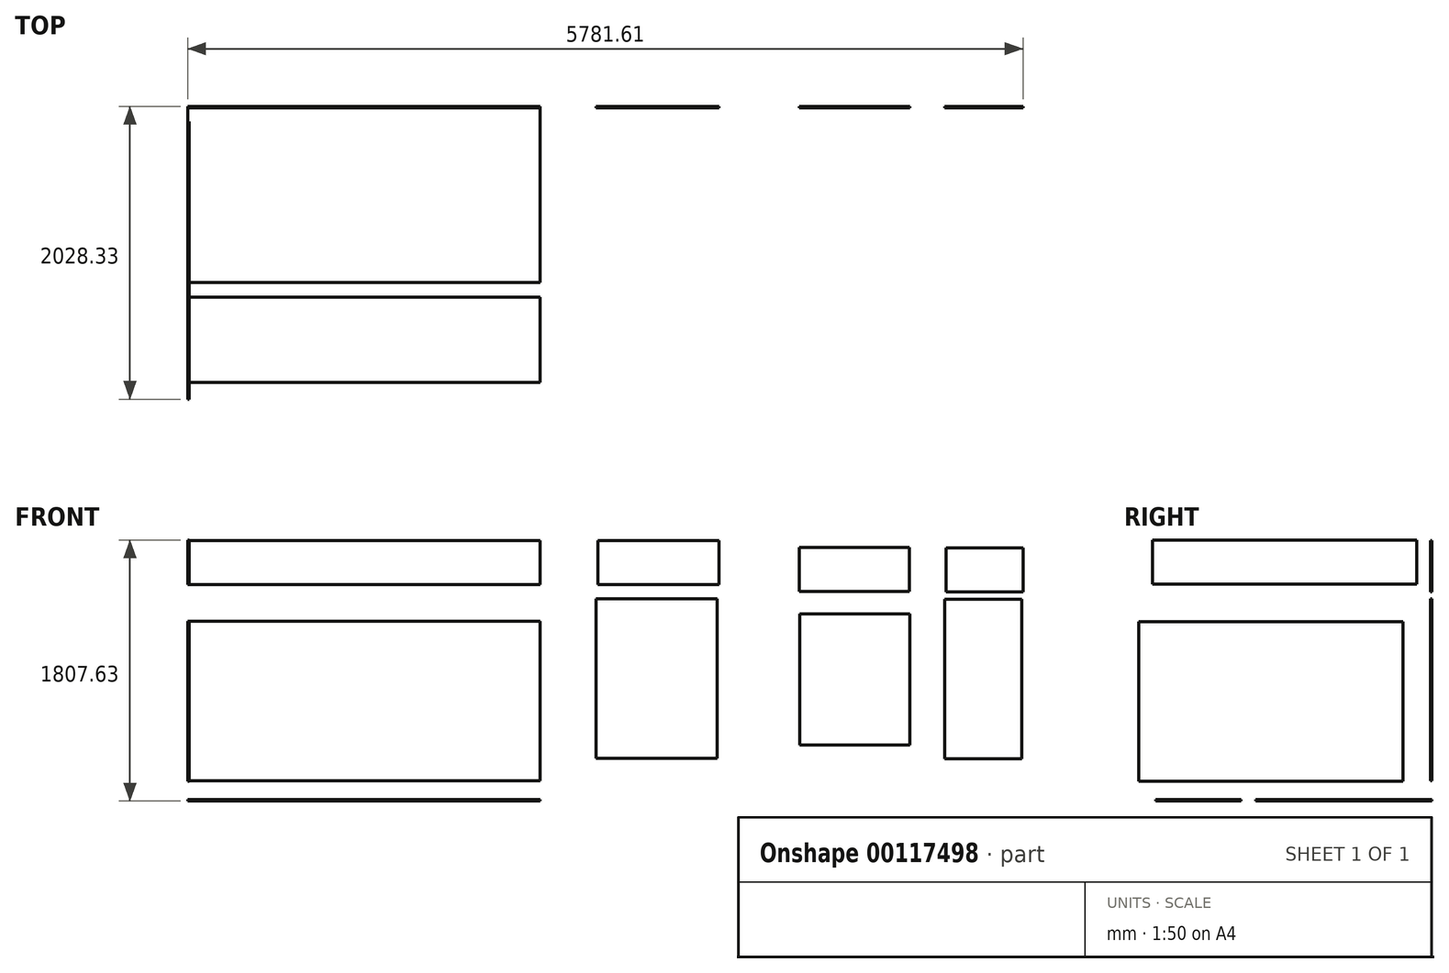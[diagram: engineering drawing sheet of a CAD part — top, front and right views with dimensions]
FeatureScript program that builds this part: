
annotation { "Feature Type Name" : "Feature", "Feature Type Description" : "" }
export const myFeature = defineFeature(function(context is Context, id is Id, definition is map)
    precondition{}
    {
        {
            var Q0;
            Q0=qCreatedBy(makeId("Top.planeOp"),FACE);
            var sketch = newSketch(context, id + "F0", { "sketchPlane" : qUnion([Q0])});
            skLineSegment(sketch, "E0.bottom", {"start": v(0, 0) * mm, "end": v(2438.4, 0) * mm});
            skLineSegment(sketch, "E0.top", {"start": v(0, -1219.2) * mm, "end": v(2438.4, -1219.2) * mm});
            skLineSegment(sketch, "E0.left", {"start": v(0, 0) * mm, "end": v(0, -1219.2) * mm});
            skLineSegment(sketch, "E0.right", {"start": v(2438.4, 0) * mm, "end": v(2438.4, -1219.2) * mm});
            skSolve(sketch);
        }
        {
            var Q0;
            Q0=makeQuery(id+"F0.imprint","IMPRINT",FACE,{"disambiguationData":[TD([[makeQuery(id+"F0.imprint","IMPRINT",EDGE,{"derivedFrom":sQuery(id+"F0.wireOp",EDGE,"E0.bottom")}),-1.0]])]});
            extrude(context, id + "F1", {"entities" : qUnion([Q0]), "depth" : 9.52 * mm});
        }
        {
            var Q0;
            Q0=qCreatedBy(makeId("Top.planeOp"),FACE);
            var sketch = newSketch(context, id + "F2", { "sketchPlane" : qUnion([Q0])});
            skLineSegment(sketch, "E1.bottom", {"start": v(0, -1320.2) * mm, "end": v(2438.4, -1320.2) * mm});
            skLineSegment(sketch, "E1.top", {"start": v(0, -1910.75) * mm, "end": v(2438.4, -1910.75) * mm});
            skLineSegment(sketch, "E1.left", {"start": v(0, -1320.2) * mm, "end": v(0, -1910.75) * mm});
            skLineSegment(sketch, "E1.right", {"start": v(2438.4, -1320.2) * mm, "end": v(2438.4, -1910.75) * mm});
            skSolve(sketch);
        }
        {
            var Q0;
            Q0=makeQuery(id+"F2.imprint","IMPRINT",FACE,{"disambiguationData":[TD([[makeQuery(id+"F2.imprint","IMPRINT",EDGE,{"derivedFrom":sQuery(id+"F2.wireOp",EDGE,"E1.bottom")}),-1.0]])]});
            extrude(context, id + "F3", {"entities" : qUnion([Q0]), "depth" : 9.52 * mm});
        }
        {
            var Q0;
            Q0=qCreatedBy(makeId("Front.planeOp"),FACE);
            var sketch = newSketch(context, id + "F4", { "sketchPlane" : qUnion([Q0])});
            skLineSegment(sketch, "E2.bottom", {"start": v(0, 139.39) * mm, "end": v(2438.4, 139.39) * mm});
            skLineSegment(sketch, "E2.top", {"start": v(0, 1244.29) * mm, "end": v(2438.4, 1244.29) * mm});
            skLineSegment(sketch, "E2.left", {"start": v(0, 139.39) * mm, "end": v(0, 1244.29) * mm});
            skLineSegment(sketch, "E2.right", {"start": v(2438.4, 139.39) * mm, "end": v(2438.4, 1244.29) * mm});
            skSolve(sketch);
        }
        {
            var Q0;
            Q0=makeQuery(id+"F4.imprint","IMPRINT",FACE,{"disambiguationData":[TD([[makeQuery(id+"F4.imprint","IMPRINT",EDGE,{"derivedFrom":sQuery(id+"F4.wireOp",EDGE,"E2.bottom")}),1.0]])]});
            extrude(context, id + "F5", {"entities" : qUnion([Q0]), "depth" : 9.52 * mm});
        }
        {
            var Q0;
            Q0=qCreatedBy(makeId("Right.planeOp"),FACE);
            var sketch = newSketch(context, id + "F6", { "sketchPlane" : qUnion([Q0])});
            skLineSegment(sketch, "E3.bottom", {"start": v(-199.53, 136.34) * mm, "end": v(-2028.33, 136.34) * mm});
            skLineSegment(sketch, "E3.top", {"start": v(-199.53, 1241.24) * mm, "end": v(-2028.33, 1241.24) * mm});
            skLineSegment(sketch, "E3.left", {"start": v(-199.53, 136.34) * mm, "end": v(-199.53, 1241.24) * mm});
            skLineSegment(sketch, "E3.right", {"start": v(-2028.33, 136.34) * mm, "end": v(-2028.33, 1241.24) * mm});
            skSolve(sketch);
        }
        {
            var Q0;
            Q0=makeQuery(id+"F6.imprint","IMPRINT",FACE,{"disambiguationData":[TD([[makeQuery(id+"F6.imprint","IMPRINT",EDGE,{"derivedFrom":sQuery(id+"F6.wireOp",EDGE,"E3.bottom")}),-1.0]])]});
            extrude(context, id + "F7", {"entities" : qUnion([Q0]), "depth" : 9.52 * mm});
        }
        {
            var Q0;
            Q0=qCreatedBy(makeId("Front.planeOp"),FACE);
            var sketch = newSketch(context, id + "F8", { "sketchPlane" : qUnion([Q0])});
            skLineSegment(sketch, "E4.bottom", {"start": v(0, 1500.5) * mm, "end": v(2438.4, 1500.5) * mm});
            skLineSegment(sketch, "E4.top", {"start": v(0, 1805.3) * mm, "end": v(2438.4, 1805.3) * mm});
            skLineSegment(sketch, "E4.left", {"start": v(0, 1500.5) * mm, "end": v(0, 1805.3) * mm});
            skLineSegment(sketch, "E4.right", {"start": v(2438.4, 1500.5) * mm, "end": v(2438.4, 1805.3) * mm});
            skSolve(sketch);
        }
        {
            var Q0;
            Q0=makeQuery(id+"F8.imprint","IMPRINT",FACE,{"disambiguationData":[TD([[makeQuery(id+"F8.imprint","IMPRINT",EDGE,{"derivedFrom":sQuery(id+"F8.wireOp",EDGE,"E4.bottom")}),1.0]])]});
            extrude(context, id + "F9", {"entities" : qUnion([Q0]), "depth" : 9.52 * mm});
        }
        {
            var Q0;
            Q0=qCreatedBy(makeId("Right.planeOp"),FACE);
            var sketch = newSketch(context, id + "F10", { "sketchPlane" : qUnion([Q0])});
            skLineSegment(sketch, "E5.bottom", {"start": v(-104.16, 1502.83) * mm, "end": v(-1932.96, 1502.83) * mm});
            skLineSegment(sketch, "E5.top", {"start": v(-104.16, 1807.63) * mm, "end": v(-1932.96, 1807.63) * mm});
            skLineSegment(sketch, "E5.left", {"start": v(-104.16, 1502.83) * mm, "end": v(-104.16, 1807.63) * mm});
            skLineSegment(sketch, "E5.right", {"start": v(-1932.96, 1502.83) * mm, "end": v(-1932.96, 1807.63) * mm});
            skSolve(sketch);
        }
        {
            var Q0;
            Q0=makeQuery(id+"F10.imprint","IMPRINT",FACE,{"disambiguationData":[TD([[makeQuery(id+"F10.imprint","IMPRINT",EDGE,{"derivedFrom":sQuery(id+"F10.wireOp",EDGE,"E5.bottom")}),-1.0]])]});
            extrude(context, id + "F11", {"entities" : qUnion([Q0]), "depth" : 9.52 * mm});
        }
        {
            var Q0;
            Q0=qCreatedBy(makeId("Front.planeOp"),FACE);
            var sketch = newSketch(context, id + "F12", { "sketchPlane" : qUnion([Q0])});
            skLineSegment(sketch, "E6.bottom", {"start": v(2827.65, 295.84) * mm, "end": v(3665.85, 295.84) * mm});
            skLineSegment(sketch, "E6.top", {"start": v(2827.65, 1400.74) * mm, "end": v(3665.85, 1400.74) * mm});
            skLineSegment(sketch, "E6.left", {"start": v(2827.65, 295.84) * mm, "end": v(2827.65, 1400.74) * mm});
            skLineSegment(sketch, "E6.right", {"start": v(3665.85, 295.84) * mm, "end": v(3665.85, 1400.74) * mm});
            skSolve(sketch);
        }
        {
            var Q0;
            Q0=makeQuery(id+"F12.imprint","IMPRINT",FACE,{"disambiguationData":[TD([[makeQuery(id+"F12.imprint","IMPRINT",EDGE,{"derivedFrom":sQuery(id+"F12.wireOp",EDGE,"E6.bottom")}),1.0]])]});
            extrude(context, id + "F13", {"entities" : qUnion([Q0]), "depth" : 9.52 * mm});
        }
        {
            var Q0;
            Q0=qCreatedBy(makeId("Front.planeOp"),FACE);
            var sketch = newSketch(context, id + "F14", { "sketchPlane" : qUnion([Q0])});
            skLineSegment(sketch, "E7.bottom", {"start": v(4236.92, 388.8) * mm, "end": v(4998.92, 388.8) * mm});
            skLineSegment(sketch, "E7.top", {"start": v(4236.92, 1296.85) * mm, "end": v(4998.92, 1296.85) * mm});
            skLineSegment(sketch, "E7.left", {"start": v(4236.92, 388.8) * mm, "end": v(4236.92, 1296.85) * mm});
            skLineSegment(sketch, "E7.right", {"start": v(4998.92, 388.8) * mm, "end": v(4998.92, 1296.85) * mm});
            skSolve(sketch);
        }
        {
            var Q0;
            Q0=makeQuery(id+"F14.imprint","IMPRINT",FACE,{"disambiguationData":[TD([[makeQuery(id+"F14.imprint","IMPRINT",EDGE,{"derivedFrom":sQuery(id+"F14.wireOp",EDGE,"E7.bottom")}),1.0]])]});
            extrude(context, id + "F15", {"entities" : qUnion([Q0]), "depth" : 9.52 * mm});
        }
        {
            var Q0;
            Q0=qCreatedBy(makeId("Front.planeOp"),FACE);
            var sketch = newSketch(context, id + "F16", { "sketchPlane" : qUnion([Q0])});
            skLineSegment(sketch, "E8.bottom", {"start": v(4233.33, 1450.39) * mm, "end": v(4995.33, 1450.39) * mm});
            skLineSegment(sketch, "E8.top", {"start": v(4233.33, 1755.19) * mm, "end": v(4995.33, 1755.19) * mm});
            skLineSegment(sketch, "E8.left", {"start": v(4233.33, 1450.39) * mm, "end": v(4233.33, 1755.19) * mm});
            skLineSegment(sketch, "E8.right", {"start": v(4995.33, 1450.39) * mm, "end": v(4995.33, 1755.19) * mm});
            skSolve(sketch);
        }
        {
            var Q0;
            Q0=makeQuery(id+"F16.imprint","IMPRINT",FACE,{"disambiguationData":[TD([[makeQuery(id+"F16.imprint","IMPRINT",EDGE,{"derivedFrom":sQuery(id+"F16.wireOp",EDGE,"E8.bottom")}),1.0]])]});
            extrude(context, id + "F17", {"entities" : qUnion([Q0]), "depth" : 9.52 * mm});
        }
        {
            var Q0;
            Q0=qCreatedBy(makeId("Front.planeOp"),FACE);
            var sketch = newSketch(context, id + "F18", { "sketchPlane" : qUnion([Q0])});
            skLineSegment(sketch, "E9.bottom", {"start": v(2839.93, 1500.6) * mm, "end": v(3678.13, 1500.6) * mm});
            skLineSegment(sketch, "E9.top", {"start": v(2839.93, 1805.4) * mm, "end": v(3678.13, 1805.4) * mm});
            skLineSegment(sketch, "E9.left", {"start": v(2839.93, 1500.6) * mm, "end": v(2839.93, 1805.4) * mm});
            skLineSegment(sketch, "E9.right", {"start": v(3678.13, 1500.6) * mm, "end": v(3678.13, 1805.4) * mm});
            skSolve(sketch);
        }
        {
            var Q0;
            Q0=makeQuery(id+"F18.imprint","IMPRINT",FACE,{"disambiguationData":[TD([[makeQuery(id+"F18.imprint","IMPRINT",EDGE,{"derivedFrom":sQuery(id+"F18.wireOp",EDGE,"E9.bottom")}),1.0]])]});
            extrude(context, id + "F19", {"entities" : qUnion([Q0]), "depth" : 9.52 * mm});
        }
        {
            var Q0;
            Q0=qCreatedBy(makeId("Front.planeOp"),FACE);
            var sketch = newSketch(context, id + "F20", { "sketchPlane" : qUnion([Q0])});
            skLineSegment(sketch, "E10.bottom", {"start": v(5248.2, 1449.3) * mm, "end": v(5781.6, 1449.3) * mm});
            skLineSegment(sketch, "E10.top", {"start": v(5248.2, 1754.1) * mm, "end": v(5781.6, 1754.1) * mm});
            skLineSegment(sketch, "E10.left", {"start": v(5248.2, 1449.3) * mm, "end": v(5248.2, 1754.1) * mm});
            skLineSegment(sketch, "E10.right", {"start": v(5781.6, 1449.3) * mm, "end": v(5781.6, 1754.1) * mm});
            skSolve(sketch);
        }
        {
            var Q0;
            Q0=makeQuery(id+"F20.imprint","IMPRINT",FACE,{"disambiguationData":[TD([[makeQuery(id+"F20.imprint","IMPRINT",EDGE,{"derivedFrom":sQuery(id+"F20.wireOp",EDGE,"E10.bottom")}),1.0]])]});
            extrude(context, id + "F21", {"entities" : qUnion([Q0]), "depth" : 9.52 * mm});
        }
        {
            var Q0;
            Q0=qCreatedBy(makeId("Front.planeOp"),FACE);
            var sketch = newSketch(context, id + "F22", { "sketchPlane" : qUnion([Q0])});
            skLineSegment(sketch, "E11.bottom", {"start": v(5238.08, 1396.07) * mm, "end": v(5771.48, 1396.07) * mm});
            skLineSegment(sketch, "E11.top", {"start": v(5238.08, 291.17) * mm, "end": v(5771.48, 291.17) * mm});
            skLineSegment(sketch, "E11.left", {"start": v(5238.08, 1396.07) * mm, "end": v(5238.08, 291.17) * mm});
            skLineSegment(sketch, "E11.right", {"start": v(5771.48, 1396.07) * mm, "end": v(5771.48, 291.17) * mm});
            skSolve(sketch);
        }
        {
            var Q0;
            Q0=makeQuery(id+"F22.imprint","IMPRINT",FACE,{"disambiguationData":[TD([[makeQuery(id+"F22.imprint","IMPRINT",EDGE,{"derivedFrom":sQuery(id+"F22.wireOp",EDGE,"E11.bottom")}),-1.0]])]});
            extrude(context, id + "F23", {"entities" : qUnion([Q0]), "depth" : 9.52 * mm});
        }
    });
